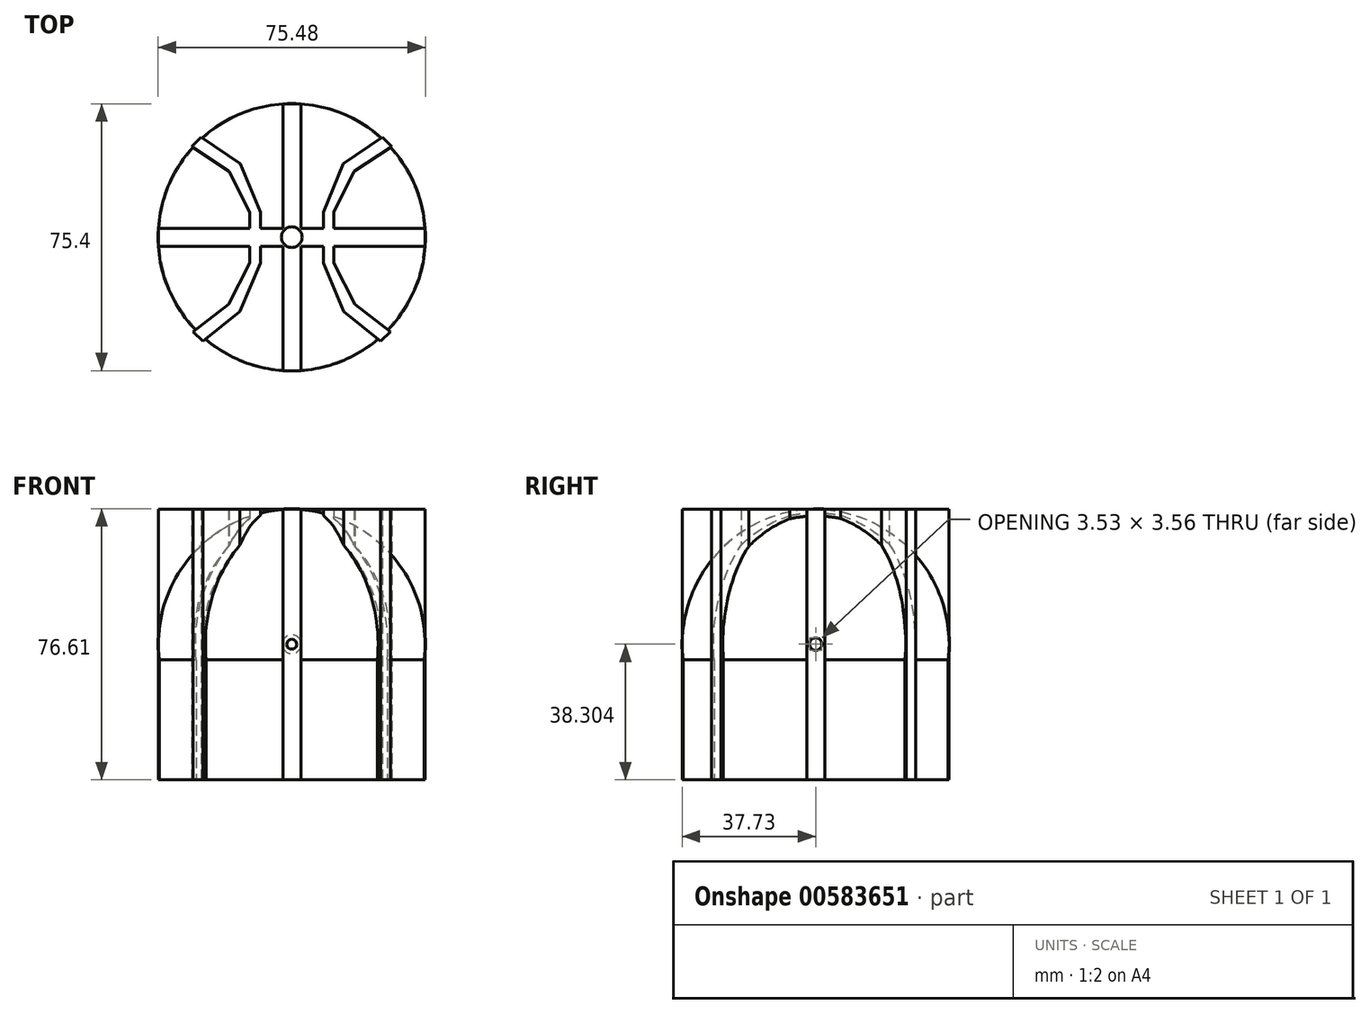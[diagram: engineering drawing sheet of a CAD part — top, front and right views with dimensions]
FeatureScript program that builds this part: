
annotation { "Feature Type Name" : "Feature", "Feature Type Description" : "" }
export const myFeature = defineFeature(function(context is Context, id is Id, definition is map)
    precondition{}
    {
        {
            var Q0;
            Q0=qCreatedBy(makeId("Top.planeOp"),FACE);
            var sketch = newSketch(context, id + "F0", { "sketchPlane" : qUnion([Q0])});
            skCircle(sketch, "E0", {"center": v(0, 0) * mm, "radius": 37.5 * mm});
            skSolve(sketch);
        }
        {
            var Q0;
            Q0=qCreatedBy(makeId("Right.planeOp"),FACE);
            var sketch = newSketch(context, id + "F1", { "sketchPlane" : qUnion([Q0])});
            skArc(sketch, "E1", {"start": v(0, 76.6) * mm, "mid": v(-37.76, 38.3) * mm, "end": v(0, 0) * mm});
            skPoint(sketch, "E1.first.point", {"position": v(0, 0) * mm});
            skPoint(sketch, "E1.second.point", {"position": v(0, 76.6) * mm});
            skPoint(sketch, "E1.third.point", {"position": v(-37.72, 36.52) * mm});
            skLineSegment(sketch, "E2", {"start": v(0, 76.6) * mm, "end": v(0, 0) * mm});
            skSolve(sketch);
        }
        {
            var Q0;
            Q0=makeQuery(id+"F1.imprint","IMPRINT",FACE,{"disambiguationData":[TD([[makeQuery(id+"F1.imprint","IMPRINT",EDGE,{"derivedFrom":sQuery(id+"F1.wireOp",EDGE,"E1")}),1.0]])]});
            var Q1;
            Q1=sQuery(id+"F0.wireOp",EDGE,"E0");
            revolve(context, id + "F2", {"entities" : qUnion([Q0]), "axis" : qUnion([Q1]), "revolveType" : RevolveType.FULL});
        }
        {
            var Q0;
            Q0=makeQuery(id+"F0.imprint","IMPRINT",FACE,{"disambiguationData":[TD([[makeQuery(id+"F0.imprint","IMPRINT",EDGE,{"derivedFrom":sQuery(id+"F0.wireOp",EDGE,"E0")}),1.0]])]});
            extrude(context, id + "F3", {"entities" : qUnion([Q0]), "operationType" : NewBodyOperationType.ADD, "depth" : 34.54 * mm, "offsetDistance" : 25.4 * mm});
        }
        {
            var Q0;
            Q0=qCreatedBy(makeId("Top.planeOp"),FACE);
            var sketch = newSketch(context, id + "F4", { "sketchPlane" : qUnion([Q0])});
            skLineSegment(sketch, "E3.2", {"start": v(25.05, -29.36) * mm, "end": v(14.63, -21.05) * mm});
            skLineSegment(sketch, "E3.3", {"start": v(14.63, -21.05) * mm, "end": v(8.9, -7.3) * mm});
            skLineSegment(sketch, "E3.4", {"start": v(8.9, -7.3) * mm, "end": v(8.9, 7) * mm});
            skLineSegment(sketch, "E3.5", {"start": v(8.9, 7) * mm, "end": v(14.52, 20.8) * mm});
            skLineSegment(sketch, "E3.6", {"start": v(14.52, 20.8) * mm, "end": v(25.55, 28.3) * mm});
            skLineSegment(sketch, "E4.2", {"start": v(27.82, -26.75) * mm, "end": v(17.82, -18.93) * mm});
            skLineSegment(sketch, "E4.3", {"start": v(17.82, -18.93) * mm, "end": v(11.9, -7.35) * mm});
            skLineSegment(sketch, "E4.4", {"start": v(11.9, -7.35) * mm, "end": v(11.9, 7) * mm});
            skLineSegment(sketch, "E4.5", {"start": v(11.9, 7) * mm, "end": v(17.66, 18.65) * mm});
            skLineSegment(sketch, "E4.6", {"start": v(17.66, 18.65) * mm, "end": v(28.27, 25.63) * mm});
            skLineSegment(sketch, "E5", {"start": v(25.55, 28.3) * mm, "end": v(28.27, 25.63) * mm});
            skLineSegment(sketch, "E6", {"start": v(14.52, 20.8) * mm, "end": v(17.66, 18.65) * mm});
            skLineSegment(sketch, "E7", {"start": v(8.9, 7) * mm, "end": v(11.9, 7) * mm});
            skLineSegment(sketch, "E8", {"start": v(8.9, -7.3) * mm, "end": v(11.9, -7.35) * mm});
            skLineSegment(sketch, "E9", {"start": v(14.63, -21.05) * mm, "end": v(17.82, -18.93) * mm});
            skLineSegment(sketch, "E10", {"start": v(25.05, -29.36) * mm, "end": v(27.82, -26.75) * mm});
            skLineSegment(sketch, "E11", {"start": v(8.9, -0.31) * mm, "end": v(8.9, 7) * mm});
            skLineSegment(sketch, "E12", {"start": v(0, 37.87) * mm, "end": v(0, -38.33) * mm});
            skLineSegment(sketch, "E13.bottom", {"start": v(2.54, -2.54) * mm, "end": v(-2.54, -2.54) * mm});
            skLineSegment(sketch, "E13.top", {"start": v(2.54, 2.54) * mm, "end": v(-2.54, 2.54) * mm});
            skLineSegment(sketch, "E13.left", {"start": v(2.54, -2.54) * mm, "end": v(2.54, 2.54) * mm});
            skLineSegment(sketch, "E13.right", {"start": v(-2.54, -2.54) * mm, "end": v(-2.54, 2.54) * mm});
            skPoint(sketch, "E13.middle", {"position": v(0, 0) * mm});
            skLineSegment(sketch, "E14.bottom", {"start": v(-2.54, 2.54) * mm, "end": v(2.54, 2.54) * mm});
            skLineSegment(sketch, "E15", {"start": v(2.54, -2.54) * mm, "end": v(2.54, -37.73) * mm});
            skLineSegment(sketch, "E16", {"start": v(2.54, -37.73) * mm, "end": v(0, -37.73) * mm});
            skLineSegment(sketch, "E17", {"start": v(2.54, 2.54) * mm, "end": v(2.54, 37.67) * mm});
            skLineSegment(sketch, "E18", {"start": v(2.54, 37.67) * mm, "end": v(0, 37.67) * mm});
            skLineSegment(sketch, "E19", {"start": v(2.54, -2.54) * mm, "end": v(37.72, -2.54) * mm});
            skLineSegment(sketch, "E20.MirrorCS", {"start": v(-14.52, 20.8) * mm, "end": v(-17.66, 18.65) * mm});
            skLineSegment(sketch, "E21.MirrorCS", {"start": v(-14.63, -21.05) * mm, "end": v(-17.82, -18.93) * mm});
            skLineSegment(sketch, "E22.MirrorCS", {"start": v(-8.9, -7.3) * mm, "end": v(-11.9, -7.35) * mm});
            skLineSegment(sketch, "E23.MirrorCS", {"start": v(-8.9, 7) * mm, "end": v(-11.9, 7) * mm});
            skLineSegment(sketch, "E24.MirrorCS", {"start": v(-25.55, 28.3) * mm, "end": v(-28.27, 25.63) * mm});
            skLineSegment(sketch, "E25.MirrorCS", {"start": v(-2.54, 37.67) * mm, "end": v(0, 37.67) * mm});
            skLineSegment(sketch, "E26.MirrorCS", {"start": v(-25.05, -29.36) * mm, "end": v(-27.82, -26.75) * mm});
            skLineSegment(sketch, "E27.MirrorCS", {"start": v(-37.72, -2.54) * mm, "end": v(-37.72, 2.54) * mm});
            skLineSegment(sketch, "E28.MirrorCS", {"start": v(-2.54, -37.73) * mm, "end": v(0, -37.73) * mm});
            skLineSegment(sketch, "E29.MirrorCS", {"start": v(-8.9, -0.31) * mm, "end": v(-8.9, 7) * mm});
            skLineSegment(sketch, "E30.MirrorCS", {"start": v(-17.82, -18.93) * mm, "end": v(-11.9, -7.35) * mm});
            skLineSegment(sketch, "E31.MirrorCS", {"start": v(-8.9, 7) * mm, "end": v(-14.52, 20.8) * mm});
            skLineSegment(sketch, "E32.MirrorCS", {"start": v(-2.54, 2.54) * mm, "end": v(-2.54, 37.67) * mm});
            skLineSegment(sketch, "E33.MirrorCS", {"start": v(-11.9, 7) * mm, "end": v(-17.66, 18.65) * mm});
            skLineSegment(sketch, "E34.MirrorCS", {"start": v(-2.54, -2.54) * mm, "end": v(-2.54, -37.73) * mm});
            skLineSegment(sketch, "E35.MirrorCS", {"start": v(-17.66, 18.65) * mm, "end": v(-28.27, 25.63) * mm});
            skLineSegment(sketch, "E36.MirrorCS", {"start": v(-37.72, 2.54) * mm, "end": v(-2.54, 2.54) * mm});
            skLineSegment(sketch, "E37.MirrorCS", {"start": v(-14.52, 20.8) * mm, "end": v(-25.55, 28.3) * mm});
            skLineSegment(sketch, "E38.MirrorCS", {"start": v(-14.63, -21.05) * mm, "end": v(-8.9, -7.3) * mm});
            skLineSegment(sketch, "E39.MirrorCS", {"start": v(-8.9, -7.3) * mm, "end": v(-8.9, 7) * mm});
            skLineSegment(sketch, "E40.MirrorCS", {"start": v(-27.82, -26.75) * mm, "end": v(-17.82, -18.93) * mm});
            skLineSegment(sketch, "E41.MirrorCS", {"start": v(-2.54, -2.54) * mm, "end": v(-37.72, -2.54) * mm});
            skLineSegment(sketch, "E42.MirrorCS", {"start": v(-25.05, -29.36) * mm, "end": v(-14.63, -21.05) * mm});
            skLineSegment(sketch, "E43.MirrorCS", {"start": v(-11.9, -7.35) * mm, "end": v(-11.9, 7) * mm});
            skLineSegment(sketch, "E44", {"start": v(2.54, 2.54) * mm, "end": v(37.72, 2.54) * mm});
            skLineSegment(sketch, "E45", {"start": v(37.72, 2.54) * mm, "end": v(37.72, -2.54) * mm});
            skLineSegment(sketch, "E46", {"start": v(2.54, 2.54) * mm, "end": v(8.9, 2.54) * mm});
            skSolve(sketch);
        }
        {
            var Q0;
            Q0 = qSketchRegion(id + "F4", true);
            extrude(context, id + "F5", {"entities" : qUnion([Q0]), "operationType" : NewBodyOperationType.ADD, "depth" : 76.45 * mm, "offsetDistance" : 25.4 * mm});
        }
    });
